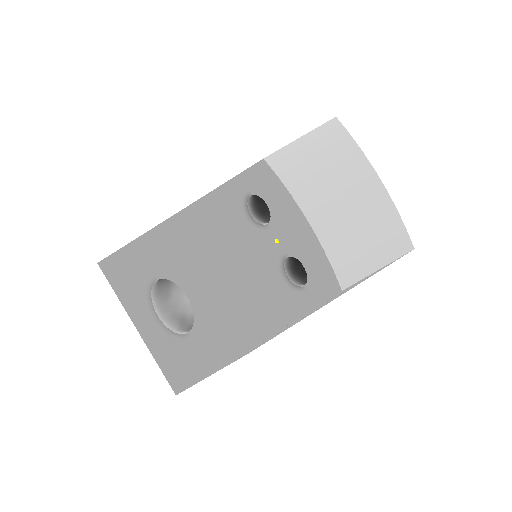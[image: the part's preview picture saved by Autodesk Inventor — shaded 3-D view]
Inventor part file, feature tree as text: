
AUTODESK INVENTOR PART (.ipt)
format: ipt  version: 2022 (Build 260153000, 153)  size: 102,912 bytes
history: native  units: mm
features: other x4, sketch x3, reference x3, extrude x1
ambient origin geometry x8: Origin, YZ Plane, XZ Plane, XY Plane, X Axis, Y Axis, Z Axis, Center Point
bodies: Volumenkörper1 (feature_tree)
feature tree (11):
  extrude  "Extrusion1"  Depth=5.9mm
  sketch  "Skizze2"  dims[d2=3.2mm]
  sketch  "Skizze3"  dims[d3=3.2mm d4=10.0mm d5=0.0mm]
  sketch  "Skizze1"  dims[d0=23.0mm d1=5.9mm]
  reference  "Referenz1"
  reference  "Referenz2"
  reference  "Referenz3"
  other  "Assembly_Matchboxscope_injectionmolded_holo.iam"
  other  "IM_Matchboxscope_Laserholder:1"
  other  "00_laserpointer_red:2"
  other  "00_mk8_nozzle_0.4STEP:1"
